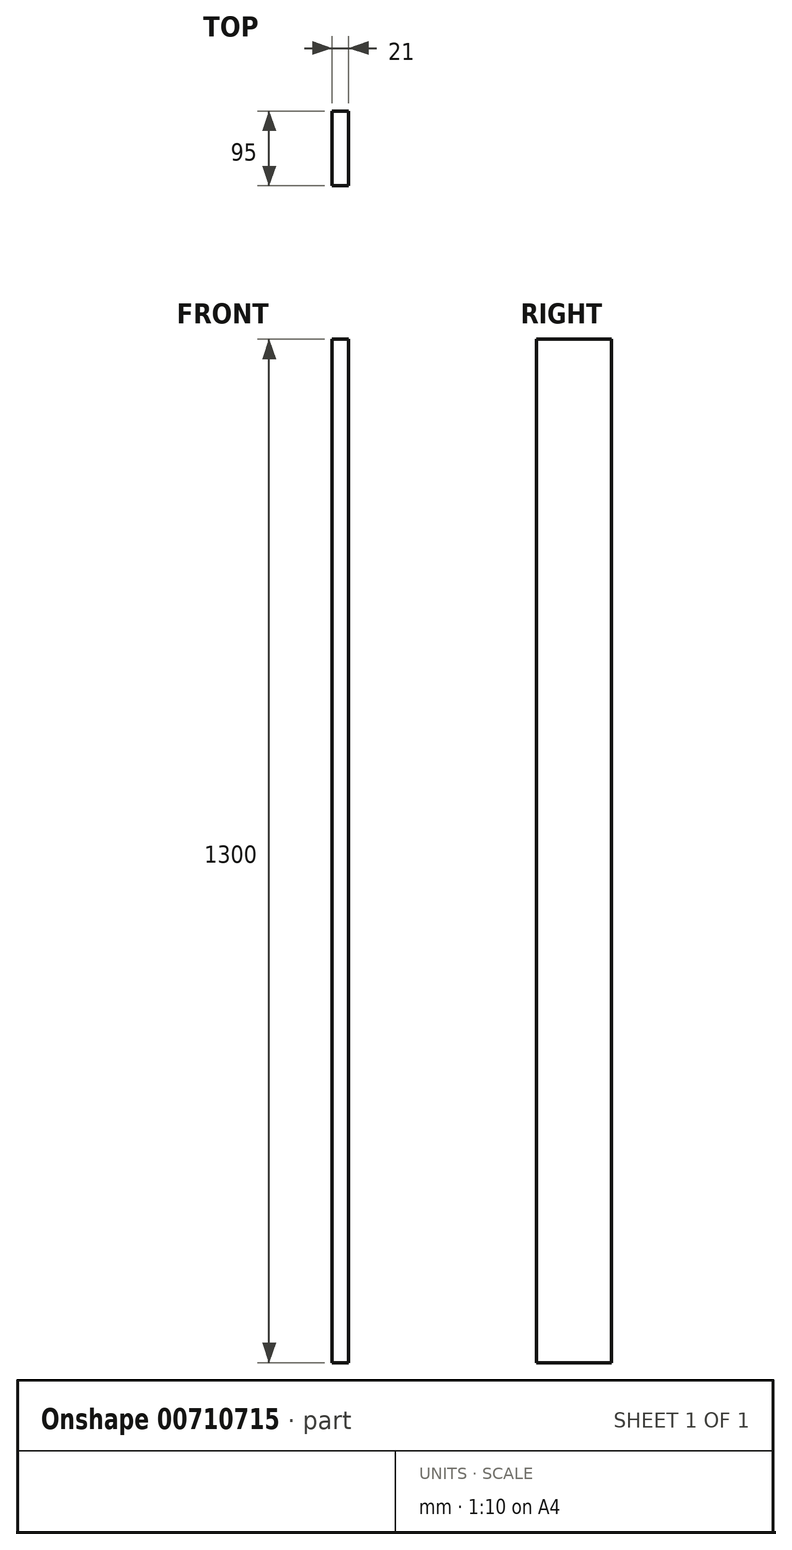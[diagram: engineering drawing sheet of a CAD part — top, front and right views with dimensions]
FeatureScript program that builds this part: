
annotation { "Feature Type Name" : "Feature", "Feature Type Description" : "" }
export const myFeature = defineFeature(function(context is Context, id is Id, definition is map)
    precondition{}
    {
        {
            assignVariable(context, id + "F0", {"name" : "l", "anyValue" : 1300});
        }
        {
            var Q0;
            Q0=qCreatedBy(makeId("Top.planeOp"),FACE);
            var sketch = newSketch(context, id + "F1", { "sketchPlane" : qUnion([Q0])});
            skLineSegment(sketch, "E0.bottom", {"start": v(0, 0) * mm, "end": v(21, 0) * mm});
            skLineSegment(sketch, "E0.top", {"start": v(0, 95) * mm, "end": v(21, 95) * mm});
            skLineSegment(sketch, "E0.left", {"start": v(0, 0) * mm, "end": v(0, 95) * mm});
            skLineSegment(sketch, "E0.right", {"start": v(21, 0) * mm, "end": v(21, 95) * mm});
            skSolve(sketch);
        }
        {
            var Q0;
            Q0=makeQuery(id+"F1.imprint","IMPRINT",FACE,{"disambiguationData":[TD([[makeQuery(id+"F1.imprint","IMPRINT",EDGE,{"derivedFrom":sQuery(id+"F1.wireOp",EDGE,"E0.bottom")}),1.0]])]});
            extrude(context, id + "F2", {"entities" : qUnion([Q0]), "depth" : (getVariable(context, 'l')) * mm, "offsetDistance" : 25 * mm});
        }
    });
